# Revit family: PRD_AR_PprTwlDpnsrs_STRATOSPaperTowelDispenser_STRX600,STRX601
name_source: partatom
category: Furniture
revit_build: Autodesk Revit 2018 (Build: 20190510_1515(x64)
units: mm (PartAtom-declared; Revit-internal decimal feet)

## family parameters
Cut with Voids When Loaded = No
Host = Face
OmniClass Number = 23.40.20.21
OmniClass Title = Toilet and Bath Specialties
Room Calculation Point = No
Shared = No

## types (2) — shared parameters
AssetType = Fixed
Color = Stainless steel
Default Elevation = 1200 mm
DispenserMaterial = PRD_AR_StainlessSteel_SatinFinished
DurationUnit = year
FillingQuantity1 = 400 towels
Finish = Satin finished
Form = Wall mounted
IfcExportAs = IfcFurnitureType
IfcExportType = NOTDEFINED
IntegralAccessories = Incl. stainless steel screws and dowels
Lock = key-lock
MainColor = Stainless steel
Manufacturer = KWC Group AG
ManufacturerName = KWC Group AG
ManufacturerURL = www.kwc.com
Material = Stainless steel
MaterialCode = Stainless steel 1.4301
NominalDepth = 134 mm
Operation = Manual
ProductInformation = https://pim.kwc.com
Style = Paper towel dispenser
SurfaceTreatment = InoxPlus (anti fingerprint)
TypeOfConsumable1 = Paper towel
TypeOfFixing = Screw
TypeOfMounting = Wall mounting
TypeOfOperation = Manual operation
URL = www.kwc.com
Uniclass2015Version = Products v1.10
Version = 1
WarrantyDurationUnit = year

## per-type parameters (varying)
| type | BIMObjectName | Category | Description | Features | FillingQuantity2 | GrossWeight | ModelNumber | NBSDescription | NBSReference | Name | NetWeight | NominalHeight | NominalLength | NominalWidth | STRX600 | STRX601 | Size | TypeOfConsumable2 | Uniclass2015Code | Uniclass2015Title |
| STRX601 | PRD_AR_DispensersAndAcceptanceUnits_CombinationPaperTowelAndSoapDispenser_STRX601 | Pr_40_70_22, Dispensers and acceptance units | Paper towel-, soap dispenser combination for wall mounting, stainless steel, surface satin finished, front with InoxPlus surface refinement for the reduction of finger marks and better cleaning characteristics (easy to clean), material thickness 1.5 mm, curved front cover, cylinder lock with KWC standard key, inspection windows on front, paper towel dispenser with loading capacity 300 - 400 pcs. of paper depending on convolution, suitable for liquid soaps and lotions, 0.8 liter soap tank, push lever, incl. stainless steel screws and dowels. | For wall mounting. Dimensions: 396 x 304 x 134 mm (W x H x D) | 0.8 liter | 5.00 kg | 2000057209 | Dispensers and acceptance units |  | Combination Paper Towel And Soap Dispenser STRX601 | 4.67 kg | 304 mm  [stored 0.997375 ft] | 396 mm  [stored 1.29921 ft] | 396 mm  [stored 1.29921 ft] | No | Yes | 396 x 304 x 134 mm | Liquid soap | Pr_40_70_22 |  |
| STRX600 | PRD_AR_PaperTowelDispensers_STRATOSPaperTowelDispenser_STRX600 | Pr_40_70_22_62, Paper towel dispensers | Paper towel dispenser for wall mounting, stainless steel, surface satin finished, front with InoxPlus surface refinement for the reduction of finger marks and better cleaning characteristics (easy to clean), material thickness 1.5 mm, curved front cover, cylinder lock with KWC standard key, inspection window on front, loading capacity 300 - 400 pcs. of paper depending on convolution, incl. stainless steel screws and dowels. | stainless steel, 1.50 mm, satin finished, wall mounting, 300x305x134 mm (WxHxD) |  | 3.86 kg | 2000057205 | Paper towel dispensers | 45-35-72/344 | STRATOS paper towel dispenser STRX600 | 3.40 kg | 305 mm  [stored 1.00066 ft] | 300 mm  [stored 0.984252 ft] | 300 mm  [stored 0.984252 ft] | Yes | No | 300 x 305 x 134 mm |  | Pr_40_70_22_62 | Paper towel dispensers |

note: column(s) folded — value = type name in every type: Model, ModelReference

note: [stored X ft] marks values corroborated as IEEE doubles in the binary element streams (Revit-internal decimal feet)

## geometry (parser evidence)
native form markers: Sweep x2
no freeform markers — native parametric forms only
